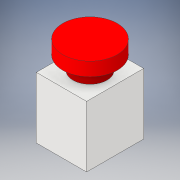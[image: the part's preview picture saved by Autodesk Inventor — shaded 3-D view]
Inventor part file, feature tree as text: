
AUTODESK INVENTOR PART (.ipt)
format: ipt  version: 2019 (Build 230136000, 136)  size: 120,832 bytes
history: native  units: mm
features: extrude x3, sketch x3
ambient origin geometry x8: Origin, YZ Plane, XZ Plane, XY Plane, X Axis, Y Axis, Z Axis, Center Point
bodies: Solid1 (feature_tree)
feature tree (6):
  extrude  "Extrusion1"  Depth=42.0mm
  extrude  "Extrusion2"  Depth=45.0mm
  extrude  "Extrusion3"  Depth=10.0mm
  sketch  "Sketch1"  dims[d0=37.0mm d1=42.0mm]
  sketch  "Sketch2"  dims[d2=45.0mm d3=0.0mm d4=25.0mm]
  sketch  "Sketch3"  dims[d5=10.0mm d6=0.0mm d7=40.0mm d8=10.0mm d9=0.0mm]
